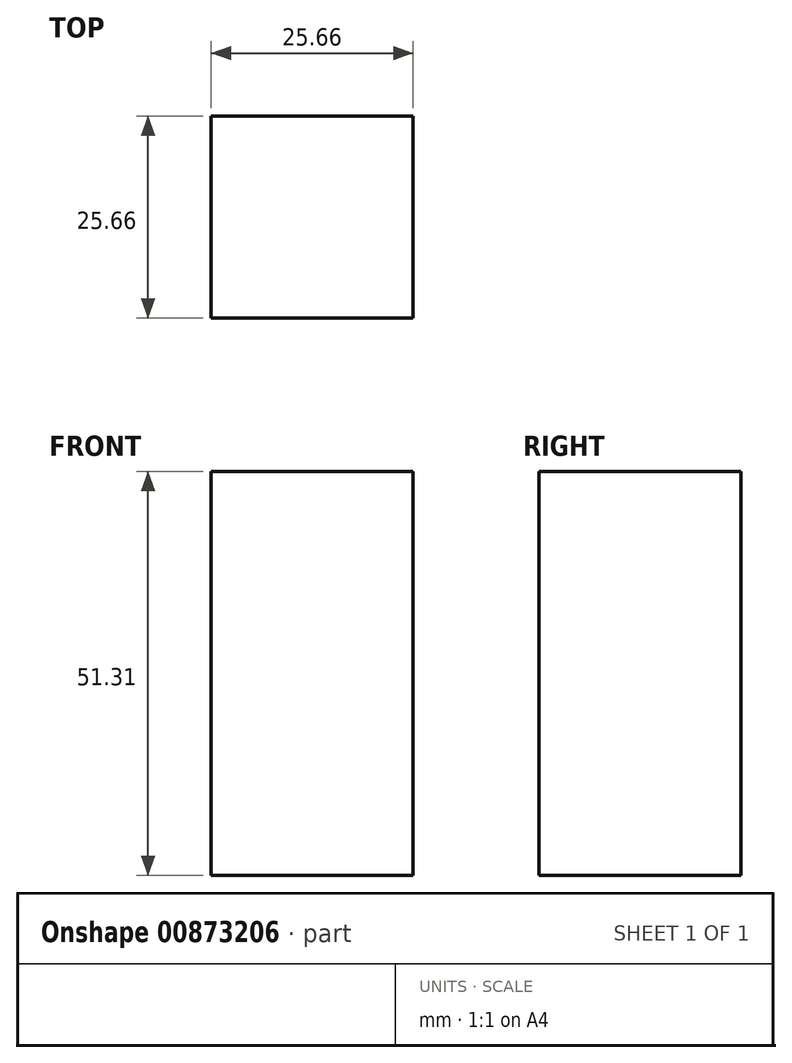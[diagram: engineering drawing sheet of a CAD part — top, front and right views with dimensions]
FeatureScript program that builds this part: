
annotation { "Feature Type Name" : "Feature", "Feature Type Description" : "" }
export const myFeature = defineFeature(function(context is Context, id is Id, definition is map)
    precondition{}
    {
        {
            var Q0;
            Q0=qCreatedBy(makeId("Front.planeOp"),FACE);
            var sketch = newSketch(context, id + "F0", { "sketchPlane" : qUnion([Q0])});
            skLineSegment(sketch, "E0", {"start": v(-55.38, -44.19) * mm, "end": v(-29.72, -44.19) * mm});
            skLineSegment(sketch, "E1", {"start": v(-29.72, -44.19) * mm, "end": v(-29.72, 7.12) * mm});
            skLineSegment(sketch, "E2", {"start": v(-29.72, 7.12) * mm, "end": v(-55.38, 7.12) * mm});
            skLineSegment(sketch, "E3", {"start": v(-55.38, 7.12) * mm, "end": v(-55.38, -44.19) * mm});
            skSolve(sketch);
        }
        {
            var Q0;
            Q0=makeQuery(id+"F0.imprint","IMPRINT",FACE,{"disambiguationData":[TD([[makeQuery(id+"F0.imprint","IMPRINT",EDGE,{"derivedFrom":sQuery(id+"F0.wireOp",EDGE,"E0")}),1.0]])]});
            extrude(context, id + "F1", {"entities" : qUnion([Q0]), "endBound" : BoundingType.SYMMETRIC, "depth" : 25.65 * mm, "offsetDistance" : 25.4 * mm});
        }
    });
